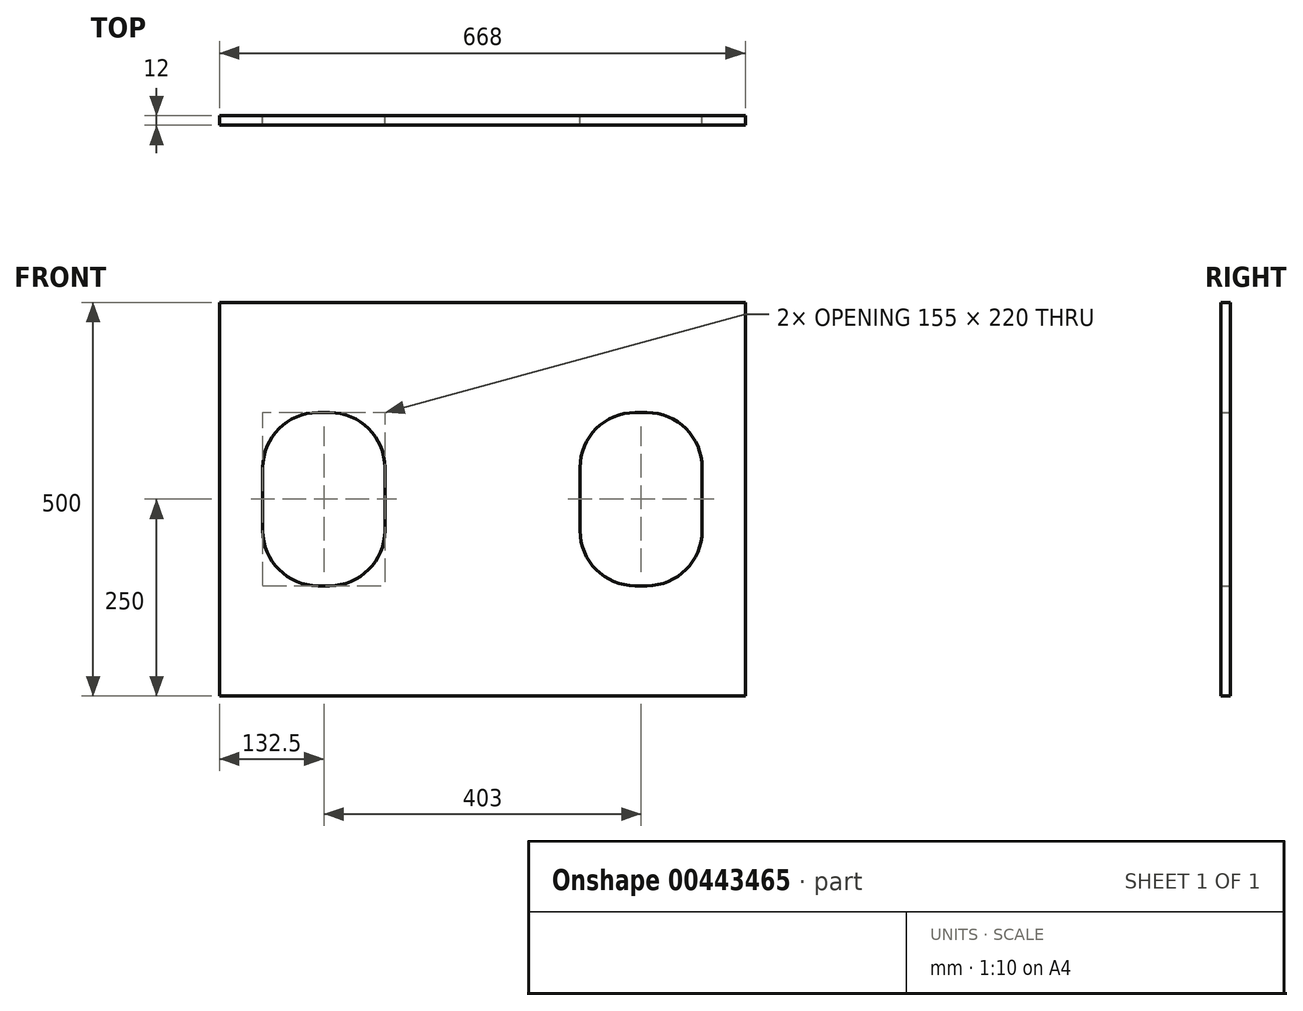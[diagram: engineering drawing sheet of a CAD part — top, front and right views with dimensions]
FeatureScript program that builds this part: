
annotation { "Feature Type Name" : "Feature", "Feature Type Description" : "" }
export const myFeature = defineFeature(function(context is Context, id is Id, definition is map)
    precondition{}
    {
        {
            var Q0;
            Q0=qCreatedBy(makeId("Front.planeOp"),FACE);
            var sketch = newSketch(context, id + "F0", { "sketchPlane" : qUnion([Q0])});
            skLineSegment(sketch, "E0.bottom", {"start": v(0, 0) * mm, "end": v(668, 0) * mm});
            skLineSegment(sketch, "E0.top", {"start": v(0, 500) * mm, "end": v(668, 500) * mm});
            skLineSegment(sketch, "E0.left", {"start": v(0, 0) * mm, "end": v(0, 500) * mm});
            skLineSegment(sketch, "E0.right", {"start": v(668, 0) * mm, "end": v(668, 500) * mm});
            skLineSegment(sketch, "E1.bottom", {"start": v(125, 140) * mm, "end": v(140, 140) * mm});
            skLineSegment(sketch, "E1.top", {"start": v(125, 360) * mm, "end": v(140, 360) * mm});
            skLineSegment(sketch, "E1.left", {"start": v(55, 210) * mm, "end": v(55, 290) * mm});
            skLineSegment(sketch, "E1.right", {"start": v(210, 210) * mm, "end": v(210, 290) * mm});
            skLineSegment(sketch, "E2.bottom", {"start": v(528, 140) * mm, "end": v(543, 140) * mm});
            skLineSegment(sketch, "E2.top", {"start": v(528, 360) * mm, "end": v(543, 360) * mm});
            skLineSegment(sketch, "E2.left", {"start": v(458, 210) * mm, "end": v(458, 290) * mm});
            skLineSegment(sketch, "E2.right", {"start": v(613, 210) * mm, "end": v(613, 290) * mm});
            skPoint(sketch, "E3.visualSharp", {"position": v(55, 360) * mm});
            skArc(sketch, "E3.filletArc", {"start": v(125, 360) * mm, "mid": v(75.5, 339.5) * mm, "end": v(55, 290) * mm});
            skPoint(sketch, "E4.visualSharp", {"position": v(210, 360) * mm});
            skArc(sketch, "E4.filletArc", {"start": v(210, 290) * mm, "mid": v(189.5, 339.5) * mm, "end": v(140, 360) * mm});
            skPoint(sketch, "E5.visualSharp", {"position": v(210, 140) * mm});
            skArc(sketch, "E5.filletArc", {"start": v(140, 140) * mm, "mid": v(189.5, 160.5) * mm, "end": v(210, 210) * mm});
            skPoint(sketch, "E6.visualSharp", {"position": v(55, 140) * mm});
            skArc(sketch, "E6.filletArc", {"start": v(55, 210) * mm, "mid": v(75.5, 160.5) * mm, "end": v(125, 140) * mm});
            skPoint(sketch, "E7.visualSharp", {"position": v(458, 140) * mm});
            skArc(sketch, "E7.filletArc", {"start": v(458, 210) * mm, "mid": v(478.5, 160.5) * mm, "end": v(528, 140) * mm});
            skPoint(sketch, "E8.visualSharp", {"position": v(613, 140) * mm});
            skArc(sketch, "E8.filletArc", {"start": v(543, 140) * mm, "mid": v(592.5, 160.5) * mm, "end": v(613, 210) * mm});
            skPoint(sketch, "E9.visualSharp", {"position": v(613, 360) * mm});
            skArc(sketch, "E9.filletArc", {"start": v(613, 290) * mm, "mid": v(592.5, 339.5) * mm, "end": v(543, 360) * mm});
            skPoint(sketch, "E10.visualSharp", {"position": v(458, 360) * mm});
            skArc(sketch, "E10.filletArc", {"start": v(528, 360) * mm, "mid": v(478.5, 339.5) * mm, "end": v(458, 290) * mm});
            skSolve(sketch);
        }
        {
            var Q0;
            Q0=makeQuery(id+"F0.imprint","IMPRINT",FACE,{"disambiguationData":[TD([[makeQuery(id+"F0.imprint","IMPRINT",EDGE,{"derivedFrom":sQuery(id+"F0.wireOp",EDGE,"E0.bottom")}),1.0]])]});
            extrude(context, id + "F1", {"entities" : qUnion([Q0]), "depth" : 12 * mm});
        }
    });
